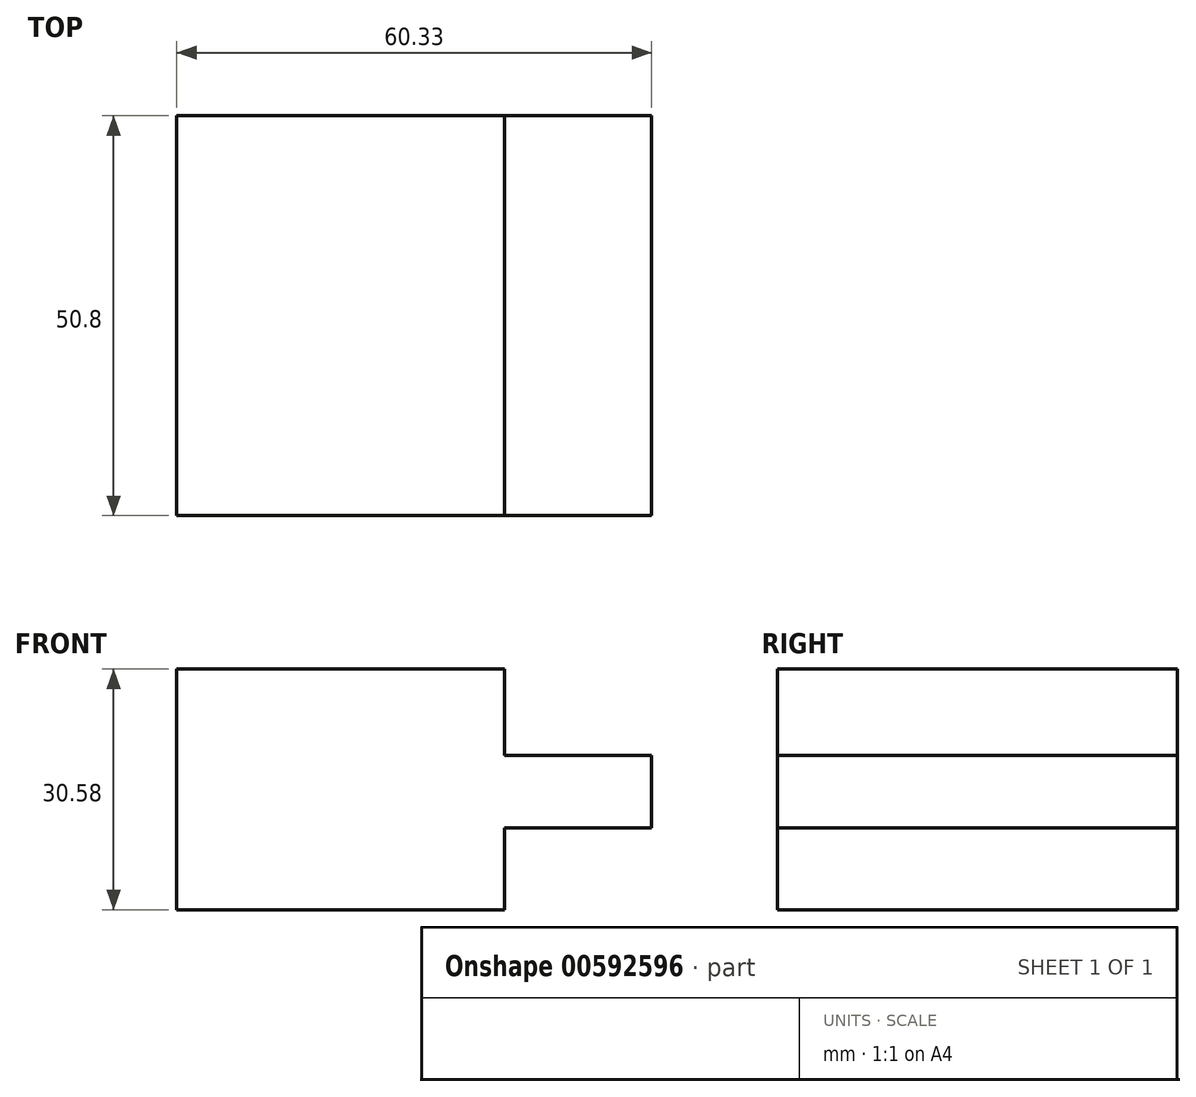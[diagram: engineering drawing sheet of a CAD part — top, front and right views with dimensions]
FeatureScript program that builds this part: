
annotation { "Feature Type Name" : "Feature", "Feature Type Description" : "" }
export const myFeature = defineFeature(function(context is Context, id is Id, definition is map)
    precondition{}
    {
        {
            var Q0;
            Q0=qCreatedBy(makeId("Front.planeOp"),FACE);
            var sketch = newSketch(context, id + "F0", { "sketchPlane" : qUnion([Q0])});
            skLineSegment(sketch, "E0", {"start": v(0, 0) * mm, "end": v(41.62, 0) * mm});
            skLineSegment(sketch, "E1", {"start": v(0, 0) * mm, "end": v(0, 30.58) * mm});
            skLineSegment(sketch, "E2", {"start": v(0, 30.58) * mm, "end": v(41.62, 30.58) * mm});
            skLineSegment(sketch, "E3", {"start": v(41.62, 30.58) * mm, "end": v(41.62, 19.6) * mm});
            skLineSegment(sketch, "E4", {"start": v(41.62, 19.6) * mm, "end": v(60.33, 19.6) * mm});
            skLineSegment(sketch, "E5", {"start": v(60.33, 19.6) * mm, "end": v(60.33, 10.4) * mm});
            skLineSegment(sketch, "E6", {"start": v(60.33, 10.4) * mm, "end": v(41.62, 10.4) * mm});
            skLineSegment(sketch, "E7", {"start": v(41.62, 10.4) * mm, "end": v(41.62, 0) * mm});
            skSolve(sketch);
        }
        {
            var Q0;
            Q0=makeQuery(id+"F0.imprint","IMPRINT",FACE,{"disambiguationData":[TD([[makeQuery(id+"F0.imprint","IMPRINT",EDGE,{"derivedFrom":sQuery(id+"F0.wireOp",EDGE,"E0")}),1.0]])]});
            extrude(context, id + "F1", {"entities" : qUnion([Q0]), "depth" : 50.8 * mm, "offsetDistance" : 25.4 * mm});
        }
    });
